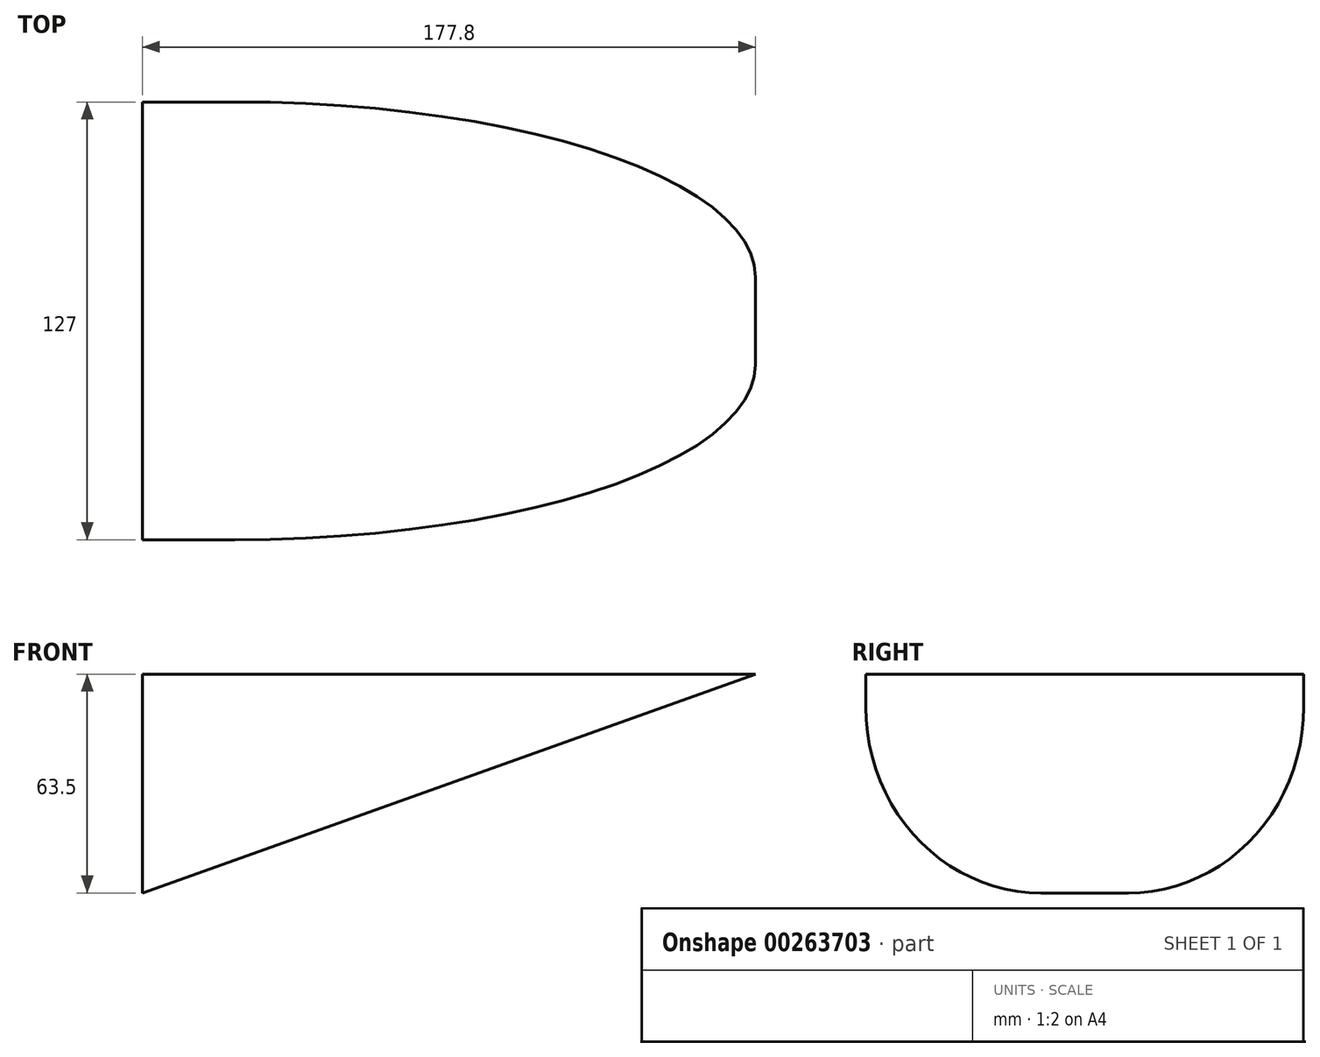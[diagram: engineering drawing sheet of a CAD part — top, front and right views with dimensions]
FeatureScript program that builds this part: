
annotation { "Feature Type Name" : "Feature", "Feature Type Description" : "" }
export const myFeature = defineFeature(function(context is Context, id is Id, definition is map)
    precondition{}
    {
        {
            var Q0;
            Q0=qCreatedBy(makeId("Front.planeOp"),FACE);
            var sketch = newSketch(context, id + "F0", { "sketchPlane" : qUnion([Q0])});
            skLineSegment(sketch, "E0", {"start": v(-37.1, 22.78) * mm, "end": v(-37.1, -40.72) * mm});
            skLineSegment(sketch, "E1", {"start": v(-37.1, 22.78) * mm, "end": v(140.7, 22.78) * mm});
            skLineSegment(sketch, "E2", {"start": v(140.7, 22.78) * mm, "end": v(-37.1, -40.72) * mm});
            skSolve(sketch);
        }
        {
            var Q0;
            Q0=makeQuery(id+"F0.imprint","IMPRINT",FACE,{"disambiguationData":[TD([[makeQuery(id+"F0.imprint","IMPRINT",EDGE,{"derivedFrom":sQuery(id+"F0.wireOp",EDGE,"E0")}),1.0]])]});
            var Q1;
            Q1=makeQuery(id+"F0.imprint","IMPRINT",FACE,{"disambiguationData":[TD([[makeQuery(id+"F0.imprint","IMPRINT",EDGE,{"derivedFrom":sQuery(id+"F0.wireOp",EDGE,"E1")}),1.0]])]});
            extrude(context, id + "F1", {"entities" : qUnion([Q0, Q1]), "endBound" : BoundingType.SYMMETRIC, "depth" : 127 * mm});
        }
        {
            var Q0;
            Q0=makeQuery(id+"F1.opExtrude","CAP_EDGE",EDGE,{"disambiguationData":[OSD([sQuery(id+"F0.wireOp",EDGE,"E2")])],"isStart":true});
            var Q1;
            Q1=makeQuery(id+"F1.opExtrude","CAP_EDGE",EDGE,{"disambiguationData":[OSD([sQuery(id+"F0.wireOp",EDGE,"E2")])],"isStart":false});
            fillet(context, id + "F2", {"entities" : qUnion([Q0, Q1]), "radius" : 50.8 * mm, "tangentPropagation" : true, "allowEdgeOverflow" : false});
        }
    });
